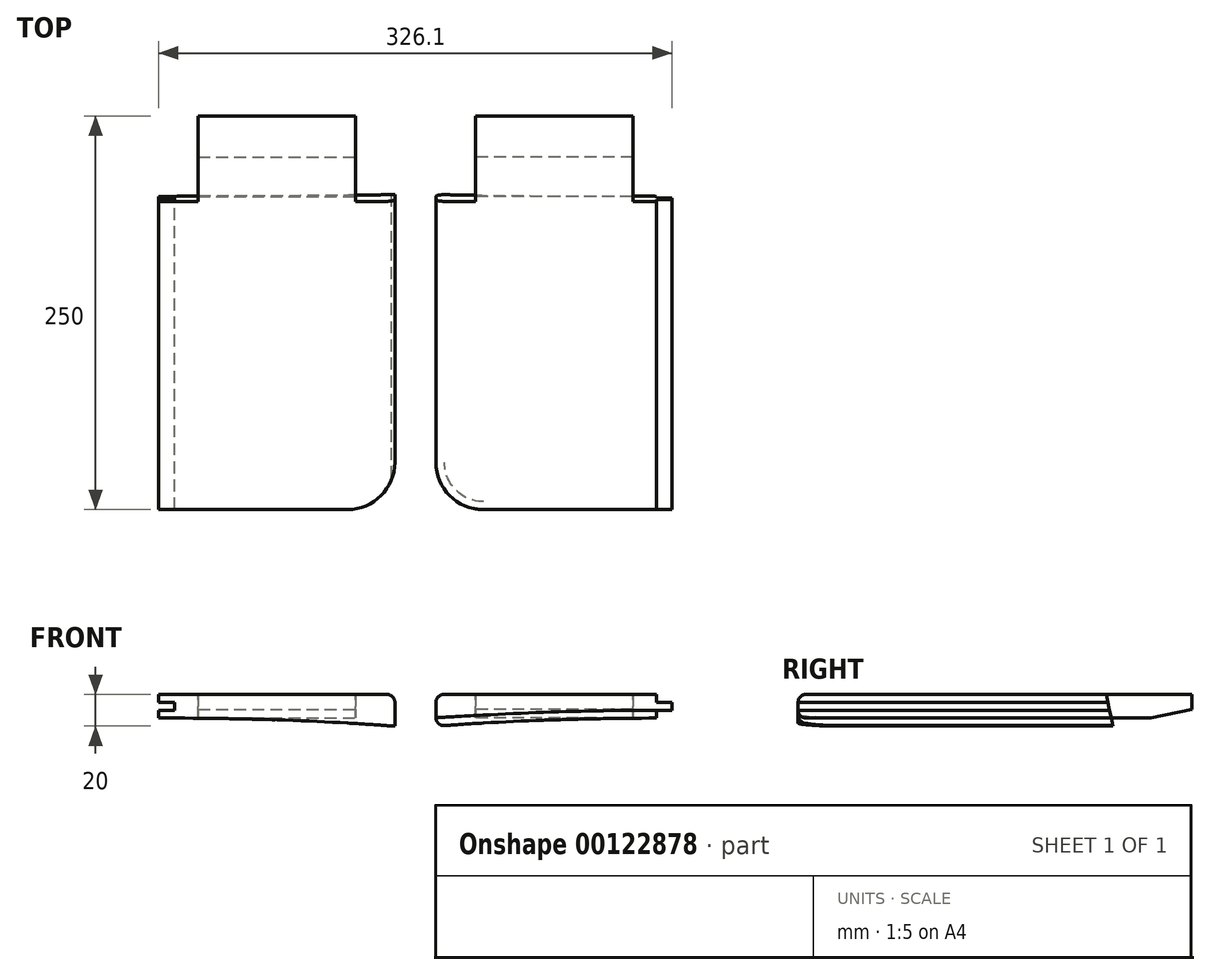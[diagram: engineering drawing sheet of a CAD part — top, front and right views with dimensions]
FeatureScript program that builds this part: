
annotation { "Feature Type Name" : "Feature", "Feature Type Description" : "" }
export const myFeature = defineFeature(function(context is Context, id is Id, definition is map)
    precondition{}
    {
        {
            var Q0;
            Q0=qCreatedBy(makeId("Front.planeOp"),FACE);
            var sketch = newSketch(context, id + "F0", { "sketchPlane" : qUnion([Q0])});
            skLineSegment(sketch, "E0", {"start": v(-150, 20) * mm, "end": v(0, 20) * mm});
            skLineSegment(sketch, "E1", {"start": v(0, 20) * mm, "end": v(0, 0) * mm});
            skLineSegment(sketch, "E2", {"start": v(0, 0) * mm, "end": v(-150, 0) * mm});
            skLineSegment(sketch, "E3", {"start": v(-150, 0) * mm, "end": v(-150, 10) * mm});
            skLineSegment(sketch, "E4", {"start": v(-150, 10) * mm, "end": v(-140, 10) * mm});
            skLineSegment(sketch, "E5", {"start": v(-140, 10) * mm, "end": v(-140, 15) * mm});
            skLineSegment(sketch, "E6", {"start": v(-140, 15) * mm, "end": v(-150, 15) * mm});
            skLineSegment(sketch, "E7", {"start": v(-150, 15) * mm, "end": v(-150, 20) * mm});
            skSolve(sketch);
        }
        {
            var Q0;
            Q0=makeQuery(id+"F0.imprint","IMPRINT",FACE,{"disambiguationData":[TD([[makeQuery(id+"F0.imprint","IMPRINT",EDGE,{"derivedFrom":sQuery(id+"F0.wireOp",EDGE,"E0")}),-1.0]])]});
            extrude(context, id + "F1", {"entities" : qUnion([Q0]), "depth" : 200 * mm});
        }
        {
            var Q0;
            Q0=makeQuery(id+"F1.opExtrude","SWEPT_FACE",FACE,{"disambiguationData":[OSD([sQuery(id+"F0.wireOp",EDGE,"E1")])]});
            var sketch = newSketch(context, id + "F2", { "sketchPlane" : qUnion([Q0])});
            skLineSegment(sketch, "E8", {"start": v(0, 0) * mm, "end": v(-4.25, 20) * mm});
            skLineSegment(sketch, "E9", {"start": v(-4.25, 20) * mm, "end": v(0, 20) * mm});
            skLineSegment(sketch, "E10", {"start": v(0, 20) * mm, "end": v(0, 0) * mm});
            skSolve(sketch);
        }
        {
            var Q0;
            Q0=makeQuery(id+"F2.imprint","IMPRINT",FACE,{"disambiguationData":[TD([[makeQuery(id+"F2.imprint","IMPRINT",EDGE,{"derivedFrom":sQuery(id+"F2.wireOp",EDGE,"E8")}),-1.0]])]});
            extrude(context, id + "F3", {"entities" : qUnion([Q0]), "operationType" : NewBodyOperationType.REMOVE, "endBound" : BoundingType.UP_TO_NEXT, "oppositeDirection" : true, "depth" : 25 * mm});
        }
        {
            var Q0;
            Q0=makeQuery(id+"F1.opExtrude","SWEPT_FACE",FACE,{"disambiguationData":[OSD([sQuery(id+"F0.wireOp",EDGE,"E1")])]});
            var sketch = newSketch(context, id + "F4", { "sketchPlane" : qUnion([Q0])});
            skLineSegment(sketch, "E11", {"start": v(-4.25, 20) * mm, "end": v(50, 20) * mm});
            skLineSegment(sketch, "E12", {"start": v(50, 20) * mm, "end": v(50, 10.54) * mm});
            skLineSegment(sketch, "E13", {"start": v(50, 10.54) * mm, "end": v(23.94, 5) * mm});
            skLineSegment(sketch, "E14", {"start": v(23.94, 5) * mm, "end": v(-1.06, 5) * mm});
            skLineSegment(sketch, "E15", {"start": v(-1.06, 5) * mm, "end": v(-4.25, 20) * mm});
            skSolve(sketch);
        }
        {
            var Q0;
            Q0=makeQuery(id+"F4.imprint","IMPRINT",FACE,{"disambiguationData":[TD([[makeQuery(id+"F4.imprint","IMPRINT",EDGE,{"derivedFrom":sQuery(id+"F4.wireOp",EDGE,"E11")}),-1.0]])]});
            extrude(context, id + "F5", {"entities" : qUnion([Q0]), "operationType" : NewBodyOperationType.ADD, "oppositeDirection" : true, "depth" : 125 * mm, "hasSecondDirection" : true, "secondDirectionOppositeDirection" : true, "secondDirectionDepth" : 25 * mm});
        }
        {
            var Q0;
            Q0=makeQuery(id+"F1.opExtrude","CAP_FACE",FACE,{"disambiguationData":[OSD([sQuery(id+"F0.wireOp",EDGE,"E0"),sQuery(id+"F0.wireOp",EDGE,"E1"),sQuery(id+"F0.wireOp",EDGE,"E2"),sQuery(id+"F0.wireOp",EDGE,"E3"),sQuery(id+"F0.wireOp",EDGE,"E4"),sQuery(id+"F0.wireOp",EDGE,"E5"),sQuery(id+"F0.wireOp",EDGE,"E6"),sQuery(id+"F0.wireOp",EDGE,"E7")])],"isStart":false});
            var sketch = newSketch(context, id + "F6", { "sketchPlane" : qUnion([Q0])});
            skEllipse(sketch, "E16", {"center": v(-145, -20) * mm, "majorRadius": 237.5 * mm, "minorRadius": 25 * mm, "majorAxis": v(1, 0)});
            skSolve(sketch);
        }
        {
            var Q0;
            {var subQ0=sQuery(id+"F6.wireOp",EDGE,"E16");var subQ1=makeQuery(id+"F1.opExtrude","CAP_EDGE",EDGE,{"disambiguationData":[OSD([sQuery(id+"F0.wireOp",EDGE,"E2")])],"isStart":false});var subQ2=makeQuery(id+"F6.imprint","INTERSECT",VERTEX,{"derivedFrom":[subQ1,subQ0]});Q0=makeQuery(id+"F6.imprint","IMPRINT",FACE,{"disambiguationData":[TD([[makeQuery(id+"F6.imprint","IMPRINT",EDGE,{"disambiguationData":[TD([[subQ2,-1.0]])],"derivedFrom":subQ0}),1.0]])]});}
            extrude(context, id + "F7", {"entities" : qUnion([Q0]), "operationType" : NewBodyOperationType.REMOVE, "endBound" : BoundingType.UP_TO_NEXT, "oppositeDirection" : true, "depth" : 25 * mm});
        }
        {
            var Q0;
            Q0=makeQuery(id+"F1.opExtrude","CAP_EDGE",EDGE,{"disambiguationData":[OSD([sQuery(id+"F0.wireOp",EDGE,"E1")])],"isStart":false});
            fillet(context, id + "F8", {"entities" : qUnion([Q0]), "radius" : 30 * mm, "tangentPropagation" : true, "allowEdgeOverflow" : false});
        }
        {
            var Q0;
            Q0=makeQuery(id+"F7.boolean.opBoolean","COPY",EDGE,{"derivedFrom":makeQuery(id+"F7.opExtrude","CAP_EDGE",EDGE,{"disambiguationData":[OSD([sQuery(id+"F6.wireOp",EDGE,"E16")])],"isStart":true})});
            var Q1;
            Q1=makeQuery(id+"F1.opExtrude","CAP_EDGE",EDGE,{"disambiguationData":[OSD([sQuery(id+"F0.wireOp",EDGE,"E0")])],"isStart":false});
            fillet(context, id + "F9", {"entities" : qUnion([Q0, Q1]), "radius" : 5 * mm, "tangentPropagation" : true, "allowEdgeOverflow" : false});
        }
        {
            var Q0;
            Q0=qCreatedBy(makeId("Front.planeOp"),FACE);
            var sketch = newSketch(context, id + "F10", { "sketchPlane" : qUnion([Q0])});
            skLineSegment(sketch, "E17", {"start": v(26.1, 0) * mm, "end": v(26.1, 20) * mm});
            skLineSegment(sketch, "E18", {"start": v(26.1, 20) * mm, "end": v(166.1, 20) * mm});
            skLineSegment(sketch, "E19", {"start": v(166.1, 20) * mm, "end": v(166.1, 15) * mm});
            skLineSegment(sketch, "E20", {"start": v(166.1, 10) * mm, "end": v(166.1, 5) * mm});
            skLineSegment(sketch, "E21", {"start": v(28.6, 0) * mm, "end": v(26.1, 0) * mm});
            skLineSegment(sketch, "E22", {"start": v(166.1, 15) * mm, "end": v(176.1, 15) * mm});
            skLineSegment(sketch, "E23", {"start": v(176.1, 15) * mm, "end": v(176.1, 10) * mm});
            skLineSegment(sketch, "E24", {"start": v(176.1, 10) * mm, "end": v(166.1, 10) * mm});
            skEllipticalArc(sketch, "E25", {});
            skPoint(sketch, "E26.orphan", {"position": v(166.1, 0) * mm});
            const initialGuessF10  = {"E25": [0.17109827281719783, -0.02, -1, 0, 0.2375, 0.025, 4.733443167408255, 5.355890089177988]};
            skSetInitialGuess(sketch, initialGuessF10);
            skSolve(sketch);
        }
        {
            var Q0;
            Q0=makeQuery(id+"F10.imprint","IMPRINT",FACE,{"disambiguationData":[TD([[makeQuery(id+"F10.imprint","IMPRINT",EDGE,{"derivedFrom":sQuery(id+"F10.wireOp",EDGE,"E17")}),-1.0]])]});
            extrude(context, id + "F11", {"entities" : qUnion([Q0]), "depth" : 200 * mm});
        }
        {
            var Q0;
            Q0=makeQuery(id+"F11.opExtrude","SWEPT_FACE",FACE,{"disambiguationData":[OSD([sQuery(id+"F10.wireOp",EDGE,"E17")])]});
            var sketch = newSketch(context, id + "F12", { "sketchPlane" : qUnion([Q0])});
            skLineSegment(sketch, "E27", {"start": v(0, 0) * mm, "end": v(4.25, 20) * mm});
            skLineSegment(sketch, "E28", {"start": v(4.25, 20) * mm, "end": v(0, 20) * mm});
            skLineSegment(sketch, "E29", {"start": v(0, 20) * mm, "end": v(0, 0) * mm});
            skSolve(sketch);
        }
        {
            var Q0;
            Q0=makeQuery(id+"F12.imprint","IMPRINT",FACE,{"disambiguationData":[TD([[makeQuery(id+"F12.imprint","IMPRINT",EDGE,{"derivedFrom":sQuery(id+"F12.wireOp",EDGE,"E27")}),1.0]])]});
            extrude(context, id + "F13", {"entities" : qUnion([Q0]), "operationType" : NewBodyOperationType.REMOVE, "endBound" : BoundingType.UP_TO_NEXT, "oppositeDirection" : true, "depth" : 25 * mm});
        }
        {
            var Q0;
            Q0=makeQuery(id+"F11.opExtrude","SWEPT_FACE",FACE,{"disambiguationData":[OSD([sQuery(id+"F10.wireOp",EDGE,"E17")])]});
            var sketch = newSketch(context, id + "F14", { "sketchPlane" : qUnion([Q0])});
            skLineSegment(sketch, "E30", {"start": v(4.25, 20) * mm, "end": v(-50, 20) * mm});
            skLineSegment(sketch, "E31", {"start": v(-50, 20) * mm, "end": v(-50, 10.54) * mm});
            skLineSegment(sketch, "E32", {"start": v(-50, 10.54) * mm, "end": v(-23.94, 5) * mm});
            skLineSegment(sketch, "E33", {"start": v(-23.94, 5) * mm, "end": v(1.06, 5) * mm});
            skLineSegment(sketch, "E34", {"start": v(1.06, 5) * mm, "end": v(4.25, 20) * mm});
            skSolve(sketch);
        }
        {
            var Q0;
            Q0=makeQuery(id+"F14.imprint","IMPRINT",FACE,{"disambiguationData":[TD([[makeQuery(id+"F14.imprint","IMPRINT",EDGE,{"derivedFrom":sQuery(id+"F14.wireOp",EDGE,"E30")}),1.0]])]});
            extrude(context, id + "F15", {"entities" : qUnion([Q0]), "operationType" : NewBodyOperationType.ADD, "oppositeDirection" : true, "depth" : 125 * mm, "hasSecondDirection" : true, "secondDirectionOppositeDirection" : true, "secondDirectionDepth" : 25 * mm});
        }
        {
            var Q0;
            Q0=makeQuery(id+"F11.opExtrude","CAP_EDGE",EDGE,{"disambiguationData":[OSD([sQuery(id+"F10.wireOp",EDGE,"E17")])],"isStart":false});
            fillet(context, id + "F16", {"entities" : qUnion([Q0]), "radius" : 30 * mm, "tangentPropagation" : true, "allowEdgeOverflow" : false});
        }
        {
            var Q0;
            Q0=makeQuery(id+"F11.opExtrude","SWEPT_EDGE",EDGE,{"disambiguationData":[OSD([sQuery(id+"F10.wireOp",EDGE,"E17"),sQuery(id+"F10.wireOp",EDGE,"E18")])]});
            var Q1;
            Q1=makeQuery(id+"F16.opFillet","BLEND_EDGE",EDGE,{"blendedFrom":[makeQuery(id+"F11.opExtrude","CAP_EDGE",EDGE,{"disambiguationData":[OSD([sQuery(id+"F10.wireOp",EDGE,"E17")])],"isStart":false}),makeQuery(id+"F11.opExtrude","SWEPT_FACE",FACE,{"disambiguationData":[OSD([sQuery(id+"F10.wireOp",EDGE,"E25")])]})],"blendedInto":[makeQuery(id+"F11.opExtrude","SWEPT_FACE",FACE,{"disambiguationData":[OSD([sQuery(id+"F10.wireOp",EDGE,"E25")])]})]});
            fillet(context, id + "F17", {"entities" : qUnion([Q0, Q1]), "radius" : 5 * mm, "tangentPropagation" : true, "allowEdgeOverflow" : false});
        }
    });
